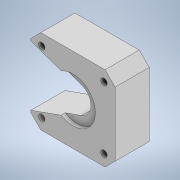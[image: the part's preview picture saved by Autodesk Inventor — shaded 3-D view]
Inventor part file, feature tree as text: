
AUTODESK INVENTOR PART (.ipt)
format: ipt  version: 2020.3 (Build 243373000, 373)  size: 138,240 bytes
history: native  units: mm
features: extrude x2, sketch x2, chamfer x1
ambient origin geometry x8: Origin, YZ Plane, XZ Plane, XY Plane, X Axis, Y Axis, Z Axis, Center Point
bodies: Solid1 (feature_tree)
feature tree (5):
  extrude  "Extrusion1"  Depth=21.0mm
  chamfer  "Chamfer1"  Distance=21.0mm
  extrude  "Extrusion2"  Depth=7.0mm
  sketch  "Sketch1"  dims[d0=21.0mm d1=21.0mm]
  sketch  "Sketch2"  dims[d2=21.0mm d3=21.0mm d4=7.0mm d5=15.5mm d6=15.5mm d7=15.5mm d8=15.5mm d9=15.5mm d10=15.5mm d11=15.5mm d12=15.5mm d13=3.2mm d14=6.0mm d15=17.0mm d16=0.0mm d17=5.0mm d18=2.0mm d19=45.0deg d20=22.4mm d21=2.0mm d22=0.0mm]
